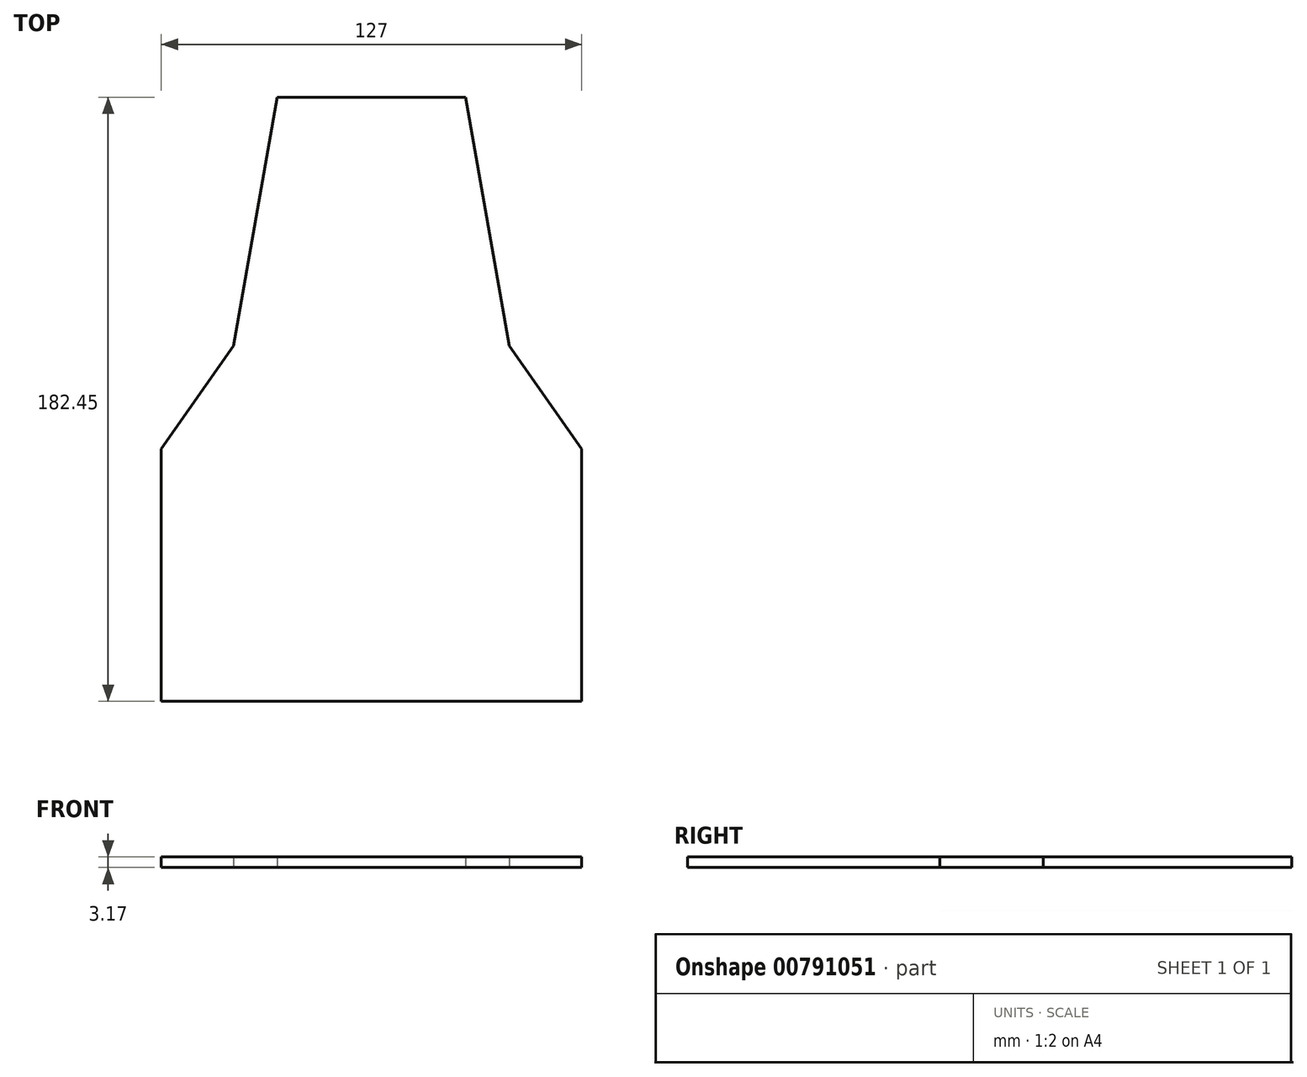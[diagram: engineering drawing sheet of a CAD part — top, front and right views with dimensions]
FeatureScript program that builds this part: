
annotation { "Feature Type Name" : "Feature", "Feature Type Description" : "" }
export const myFeature = defineFeature(function(context is Context, id is Id, definition is map)
    precondition{}
    {
        {
            var Q0;
            Q0=qCreatedBy(makeId("Top.planeOp"),FACE);
            var sketch = newSketch(context, id + "F0", { "sketchPlane" : qUnion([Q0])});
            skLineSegment(sketch, "E0", {"start": v(-84.1, -63.5) * mm, "end": v(42.9, -63.5) * mm});
            skLineSegment(sketch, "E1", {"start": v(-84.1, -63.5) * mm, "end": v(-84.1, 12.7) * mm});
            skLineSegment(sketch, "E2", {"start": v(42.9, -63.5) * mm, "end": v(42.9, 12.7) * mm});
            skLineSegment(sketch, "E3", {"start": v(-84.1, 12.7) * mm, "end": v(-62.24, 43.9) * mm});
            skLineSegment(sketch, "E4", {"start": v(42.9, 12.7) * mm, "end": v(21.05, 43.9) * mm});
            skLineSegment(sketch, "E5", {"start": v(-62.24, 43.9) * mm, "end": v(21.05, 43.9) * mm});
            skLineSegment(sketch, "E6", {"start": v(-84.1, -63.5) * mm, "end": v(-84.1, -50.8) * mm});
            skLineSegment(sketch, "E7", {"start": v(-84.1, 12.7) * mm, "end": v(-84.1, 0) * mm});
            skLineSegment(sketch, "E8", {"start": v(-84.1, 0) * mm, "end": v(-80.92, 0) * mm});
            skLineSegment(sketch, "E9", {"start": v(-80.92, 0) * mm, "end": v(-80.92, -50.8) * mm});
            skLineSegment(sketch, "E10", {"start": v(-80.92, -50.8) * mm, "end": v(-84.1, -50.8) * mm});
            skLineSegment(sketch, "E11", {"start": v(42.9, -63.5) * mm, "end": v(42.9, -50.8) * mm});
            skLineSegment(sketch, "E12", {"start": v(42.9, 12.7) * mm, "end": v(42.9, 0) * mm});
            skLineSegment(sketch, "E13", {"start": v(42.9, 0) * mm, "end": v(39.73, 0) * mm});
            skLineSegment(sketch, "E14", {"start": v(39.73, 0) * mm, "end": v(39.73, -50.8) * mm});
            skLineSegment(sketch, "E15", {"start": v(39.73, -50.8) * mm, "end": v(42.9, -50.8) * mm});
            skLineSegment(sketch, "E16", {"start": v(-62.24, 43.9) * mm, "end": v(-49.01, 118.95) * mm});
            skLineSegment(sketch, "E17", {"start": v(21.05, 43.9) * mm, "end": v(7.82, 118.95) * mm});
            skLineSegment(sketch, "E18", {"start": v(-49.01, 118.95) * mm, "end": v(7.82, 118.95) * mm});
            skPoint(sketch, "E19", {"position": v(-20.6, 118.95) * mm});
            skPoint(sketch, "E20", {"position": v(-20.6, -63.5) * mm});
            skLineSegment(sketch, "E21", {"start": v(-20.6, 118.95) * mm, "end": v(-20.6, -63.5) * mm});
            skSolve(sketch);
        }
        {
            var Q0;
            Q0 = qSketchRegion(id + "F0", true);
            extrude(context, id + "F1", {"entities" : qUnion([Q0]), "depth" : 3.17 * mm, "offsetDistance" : 25.4 * mm});
        }
    });
